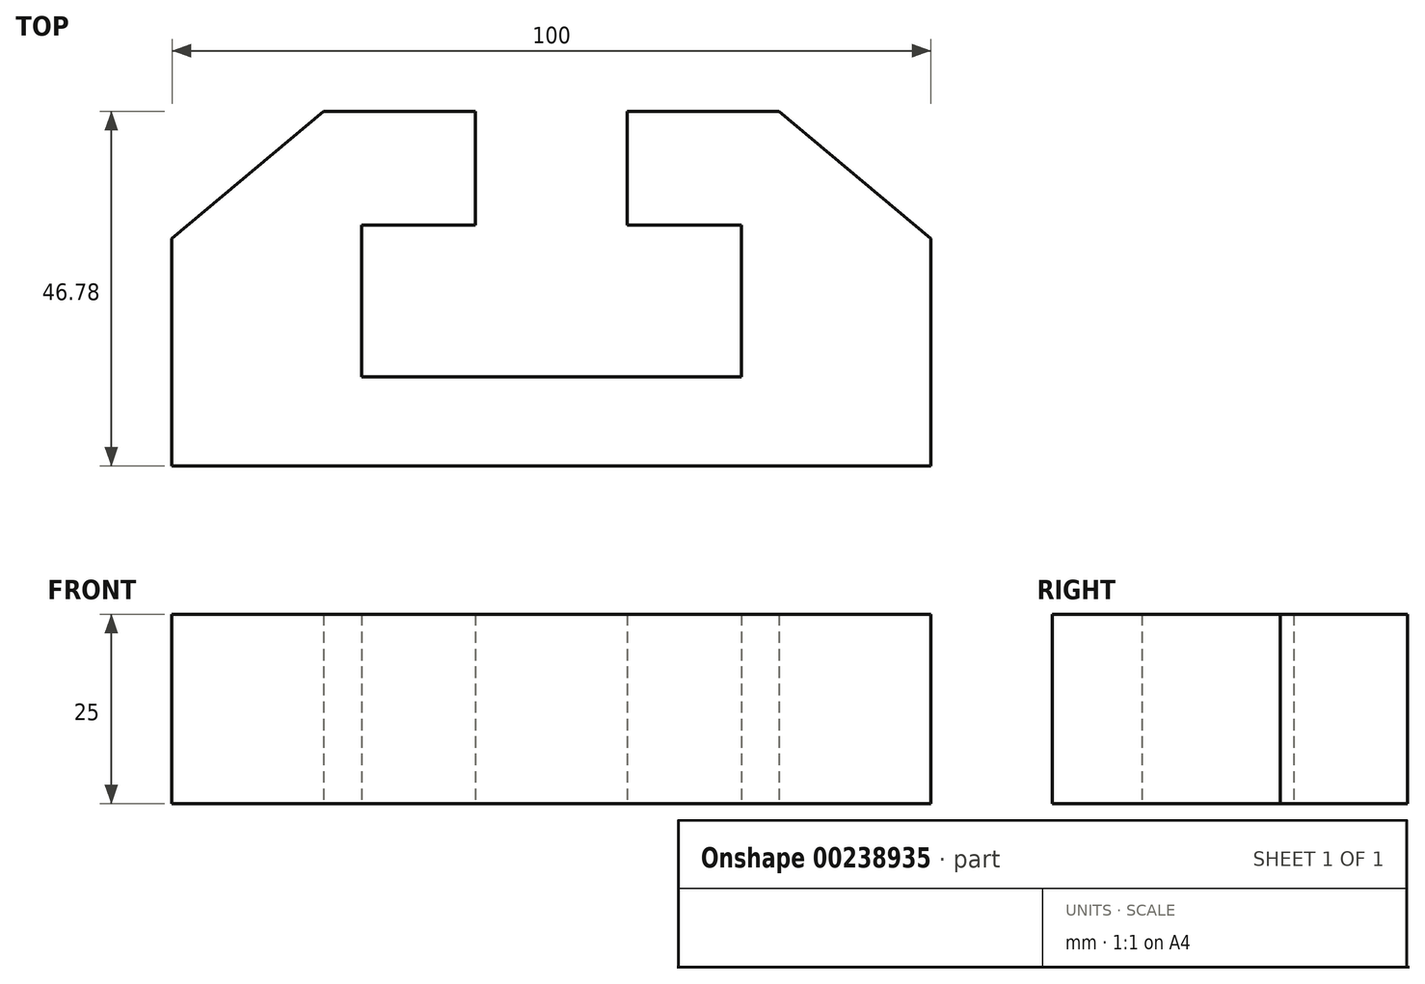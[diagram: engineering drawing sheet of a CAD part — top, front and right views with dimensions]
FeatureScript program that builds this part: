
annotation { "Feature Type Name" : "Feature", "Feature Type Description" : "" }
export const myFeature = defineFeature(function(context is Context, id is Id, definition is map)
    precondition{}
    {
        {
            var Q0;
            Q0=qCreatedBy(makeId("Top.planeOp"),FACE);
            var sketch = newSketch(context, id + "F0", { "sketchPlane" : qUnion([Q0])});
            skLineSegment(sketch, "E0", {"start": v(-54.72, -30) * mm, "end": v(45.28, -30) * mm});
            skLineSegment(sketch, "E1", {"start": v(-54.72, -30) * mm, "end": v(-54.72, 0) * mm});
            skLineSegment(sketch, "E2", {"start": v(45.28, -30) * mm, "end": v(45.28, 0) * mm});
            skLineSegment(sketch, "E3", {"start": v(-54.72, 0) * mm, "end": v(-29.72, 0) * mm});
            skLineSegment(sketch, "E4", {"start": v(45.28, 0) * mm, "end": v(20.28, 0) * mm});
            skLineSegment(sketch, "E5", {"start": v(-54.72, 0) * mm, "end": v(-34.72, 16.78) * mm});
            skLineSegment(sketch, "E6", {"start": v(45.28, 0) * mm, "end": v(25.28, 16.78) * mm});
            skLineSegment(sketch, "E7", {"start": v(-34.72, 16.78) * mm, "end": v(-14.72, 16.78) * mm});
            skLineSegment(sketch, "E8", {"start": v(25.28, 16.78) * mm, "end": v(5.28, 16.78) * mm});
            skLineSegment(sketch, "E9", {"start": v(-14.72, 16.78) * mm, "end": v(-14.72, 1.78) * mm});
            skLineSegment(sketch, "E10", {"start": v(5.28, 16.78) * mm, "end": v(5.28, 1.78) * mm});
            skLineSegment(sketch, "E11", {"start": v(-14.72, 1.78) * mm, "end": v(-29.72, 1.78) * mm});
            skLineSegment(sketch, "E12", {"start": v(5.28, 1.78) * mm, "end": v(20.28, 1.78) * mm});
            skLineSegment(sketch, "E13", {"start": v(-29.72, 1.78) * mm, "end": v(-29.72, -18.22) * mm});
            skLineSegment(sketch, "E14", {"start": v(20.28, 1.78) * mm, "end": v(20.28, -18.22) * mm});
            skLineSegment(sketch, "E15", {"start": v(-29.72, -18.22) * mm, "end": v(20.28, -18.22) * mm});
            skLineSegment(sketch, "E16", {"start": v(42.14, -15) * mm, "end": v(40.4, -15) * mm});
            skPoint(sketch, "E16.startSnap0", {"position": v(45.28, -15) * mm});
            skSolve(sketch);
        }
        {
            var Q0;
            Q0 = qSketchRegion(id + "F0", true);
            extrude(context, id + "F1", {"entities" : qUnion([Q0]), "depth" : 25 * mm});
        }
    });
